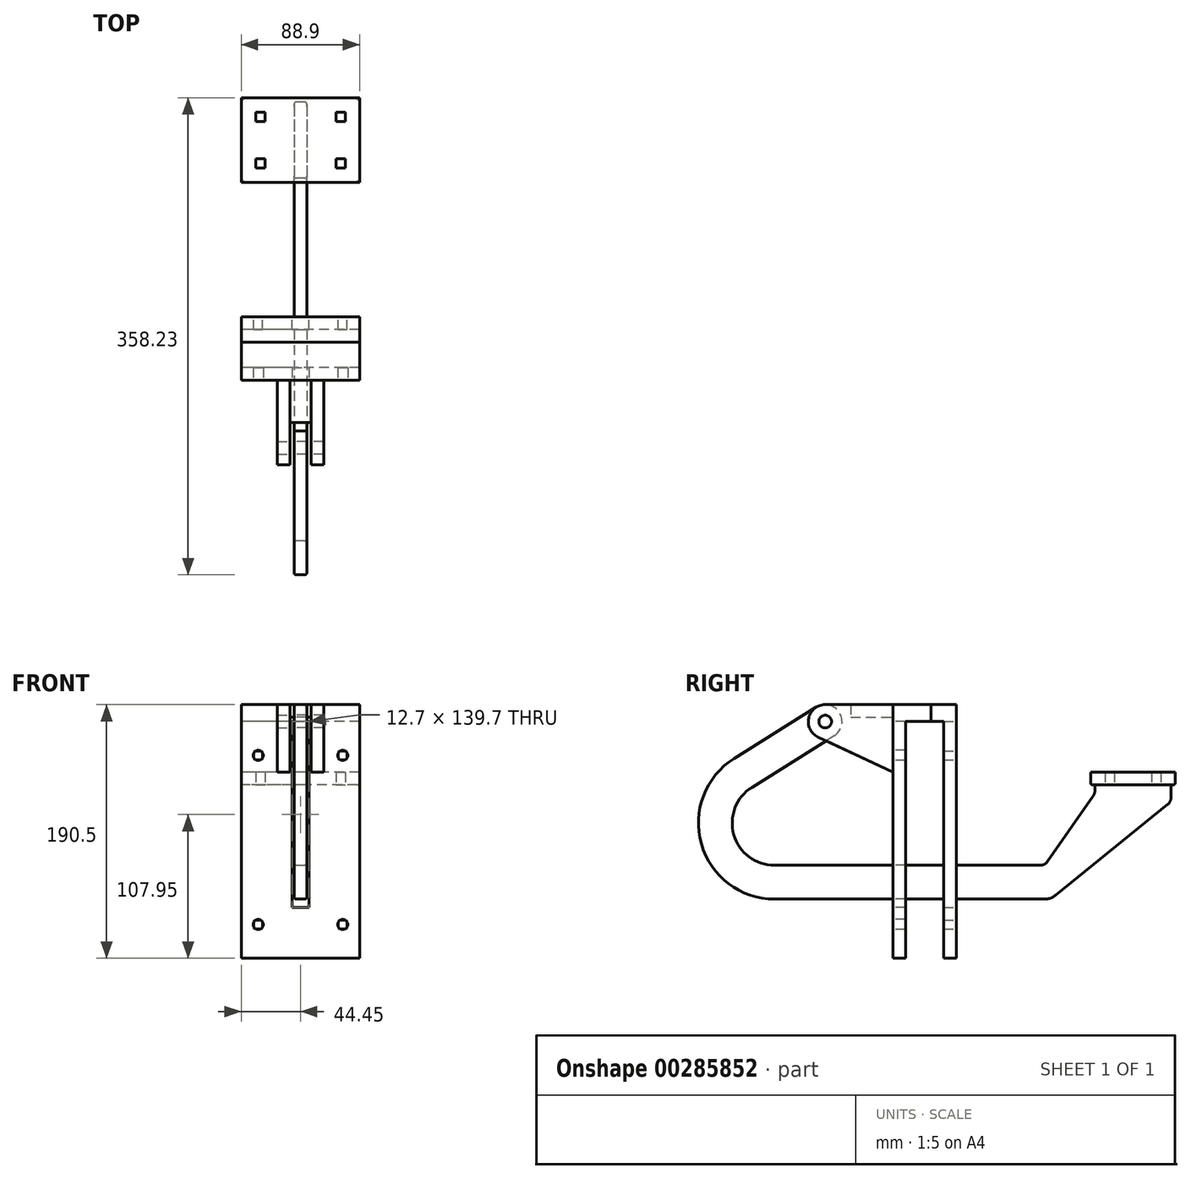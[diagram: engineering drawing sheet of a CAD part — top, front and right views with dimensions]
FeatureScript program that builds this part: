
annotation { "Feature Type Name" : "Feature", "Feature Type Description" : "" }
export const myFeature = defineFeature(function(context is Context, id is Id, definition is map)
    precondition{}
    {
        {
            var Q0;
            Q0=qCreatedBy(makeId("Right.planeOp"),FACE);
            var sketch = newSketch(context, id + "F0", { "sketchPlane" : qUnion([Q0])});
            skLineSegment(sketch, "E0.bottom", {"start": v(165.1, -133.35) * mm, "end": v(-38.1, -133.35) * mm});
            skLineSegment(sketch, "E0.top", {"start": v(161.65, -107.95) * mm, "end": v(-38.1, -107.95) * mm});
            skLineSegment(sketch, "E0.left", {"start": v(169.6, -133.35) * mm, "end": v(169.6, -132.53) * mm});
            skPoint(sketch, "E0.middle", {"position": v(0, 0) * mm});
            skLineSegment(sketch, "E1.bottom", {"start": v(262.98, -47.62) * mm, "end": v(199.48, -47.62) * mm});
            skLineSegment(sketch, "E1.top", {"start": v(262.98, -38.1) * mm, "end": v(199.48, -38.1) * mm});
            skLineSegment(sketch, "E1.left", {"start": v(262.98, -47.62) * mm, "end": v(262.98, -38.1) * mm});
            skLineSegment(sketch, "E1.right", {"start": v(199.48, -47.62) * mm, "end": v(199.48, -38.1) * mm});
            skPoint(sketch, "E1.middle", {"position": v(231.23, -42.86) * mm});
            skLineSegment(sketch, "E2.bottom", {"start": v(60.33, -177.8) * mm, "end": v(50.8, -177.8) * mm});
            skLineSegment(sketch, "E2.top", {"start": v(60.33, 12.7) * mm, "end": v(50.8, 12.7) * mm});
            skLineSegment(sketch, "E2.left", {"start": v(60.33, -177.8) * mm, "end": v(60.33, 12.7) * mm});
            skLineSegment(sketch, "E2.right", {"start": v(50.8, -177.8) * mm, "end": v(50.8, 12.7) * mm});
            skPoint(sketch, "E2.middle", {"position": v(55.56, -82.55) * mm});
            skArc(sketch, "E3", {"start": v(6.73, -10.77) * mm, "mid": v(-0.74, 12.68) * mm, "end": v(-5.43, -11.48) * mm});
            skLineSegment(sketch, "E4", {"start": v(0, 12.7) * mm, "end": v(50.8, 12.7) * mm});
            skLineSegment(sketch, "E5", {"start": v(50.8, -38.1) * mm, "end": v(-5.43, -11.48) * mm});
            skLineSegment(sketch, "E6.0", {"start": v(6.73, -10.77) * mm, "end": v(-54.92, -49.27) * mm});
            skLineSegment(sketch, "E7", {"start": v(257.45, -62.23) * mm, "end": v(173.1, -130.52) * mm});
            skPoint(sketch, "E8.visualSharp", {"position": v(169.6, -133.35) * mm});
            skArc(sketch, "E8.filletArc", {"start": v(165.1, -133.35) * mm, "mid": v(169.34, -132.62) * mm, "end": v(173.1, -130.52) * mm});
            skLineSegment(sketch, "E9", {"start": v(166.85, -105.24) * mm, "end": v(201.51, -55.61) * mm});
            skPoint(sketch, "E10.visualSharp", {"position": v(164.96, -107.95) * mm});
            skArc(sketch, "E10.filletArc", {"start": v(161.65, -107.95) * mm, "mid": v(164.58, -107.23) * mm, "end": v(166.85, -105.24) * mm});
            skLineSegment(sketch, "E11.bottom", {"start": v(50.8, 3.18) * mm, "end": v(19.05, 3.18) * mm});
            skLineSegment(sketch, "E11.top", {"start": v(50.8, 12.7) * mm, "end": v(19.05, 12.7) * mm});
            skLineSegment(sketch, "E11.left", {"start": v(50.8, 3.18) * mm, "end": v(50.8, 12.7) * mm});
            skLineSegment(sketch, "E11.right", {"start": v(19.05, 3.18) * mm, "end": v(19.05, 12.7) * mm});
            skPoint(sketch, "E11.middle", {"position": v(34.93, 7.94) * mm});
            skLineSegment(sketch, "E12", {"start": v(-6.73, 10.77) * mm, "end": v(-68.37, -27.73) * mm});
            skPoint(sketch, "E13.visualSharp", {"position": v(-148.88, -107.95) * mm});
            skArc(sketch, "E13.filletArc", {"start": v(-54.92, -49.27) * mm, "mid": v(-68.62, -84.95) * mm, "end": v(-38.1, -107.95) * mm});
            skPoint(sketch, "E14.visualSharp", {"position": v(-237.5, -133.35) * mm});
            skArc(sketch, "E14.filletArc", {"start": v(-68.37, -27.73) * mm, "mid": v(-93.04, -91.95) * mm, "end": v(-38.1, -133.35) * mm});
            skLineSegment(sketch, "E15", {"start": v(60.33, 0) * mm, "end": v(79.38, 0) * mm});
            skLineSegment(sketch, "E16", {"start": v(79.38, 0) * mm, "end": v(79.38, 12.7) * mm});
            skLineSegment(sketch, "E17", {"start": v(79.38, 12.7) * mm, "end": v(60.33, 12.7) * mm});
            skLineSegment(sketch, "E18", {"start": v(187.89, -47.62) * mm, "end": v(274.63, -47.62) * mm, "construction": true});
            skLineSegment(sketch, "E19", {"start": v(259.8, -57.3) * mm, "end": v(259.8, -47.62) * mm});
            skLineSegment(sketch, "E20", {"start": v(202.66, -51.98) * mm, "end": v(202.66, -47.62) * mm});
            skLineSegment(sketch, "E21", {"start": v(202.66, -47.62) * mm, "end": v(199.48, -47.62) * mm, "construction": true});
            skPoint(sketch, "E22.visualSharp", {"position": v(259.8, -60.32) * mm});
            skArc(sketch, "E22.filletArc", {"start": v(257.45, -62.23) * mm, "mid": v(259.19, -60.03) * mm, "end": v(259.8, -57.3) * mm});
            skPoint(sketch, "E23.visualSharp", {"position": v(202.66, -53.97) * mm});
            skArc(sketch, "E23.filletArc", {"start": v(201.51, -55.61) * mm, "mid": v(202.36, -53.88) * mm, "end": v(202.66, -51.98) * mm});
            skCircle(sketch, "E24", {"center": v(0, 0) * mm, "radius": 4.78 * mm});
            skSolve(sketch);
        }
        {
            var Q0;
            {var subQ12=sQuery(id+"F0.wireOp",EDGE,"ojWnpXek-w9QP-OmrP-CbvC-UmweZ5DEQAdM");Q0=makeQuery(id+"F0.imprint","IMPRINT",FACE,{"disambiguationData":[TD([[makeQuery(id+"F0.imprint","IMPRINT",EDGE,{"derivedFrom":subQ12}),1.0]])]});}
            var Q1;
            Q1=makeQuery(id+"F0.imprint","IMPRINT",FACE,{"disambiguationData":[TD([[makeQuery(id+"F0.imprint","IMPRINT",EDGE,{"derivedFrom":sQuery(id+"F0.wireOp",EDGE,"ZWXedtB1-B3w1-zQnL-7TSo-fpOSPy3oLPJk")}),-1.0]])]});
            var Q2;
            {var subQ5=sQuery(id+"F0.wireOp",EDGE,"zfqev4Cs-Zl6h-Keqt-t5Zp-NvnRYcSyTW9s");Q2=makeQuery(id+"F0.imprint","IMPRINT",FACE,{"disambiguationData":[TD([[makeQuery(id+"F0.imprint","IMPRINT",EDGE,{"derivedFrom":subQ5}),-1.0]])]});}
            var Q3;
            {var subQ0=sQuery(id+"F0.wireOp",EDGE,"E2.left");var subQ1=sQuery(id+"F0.wireOp",EDGE,"E0.bottom");var subQ2=makeQuery(id+"F0.imprint","INTERSECT",VERTEX,{"derivedFrom":[subQ1,subQ0]});Q3=makeQuery(id+"F0.imprint","IMPRINT",FACE,{"disambiguationData":[TD([[makeQuery(id+"F0.imprint","IMPRINT",EDGE,{"disambiguationData":[TD([[subQ2,-1.0]])],"derivedFrom":subQ1}),-1.0]])]});}
            var Q4;
            {var subQ7=sQuery(id+"F0.wireOp",EDGE,"E12");Q4=makeQuery(id+"F0.imprint","IMPRINT",FACE,{"disambiguationData":[TD([[makeQuery(id+"F0.imprint","IMPRINT",EDGE,{"derivedFrom":subQ7}),1.0]])]});}
            var Q5;
            {var subQ4=sQuery(id+"F0.wireOp",EDGE,"E7");Q5=makeQuery(id+"F0.imprint","IMPRINT",FACE,{"disambiguationData":[TD([[makeQuery(id+"F0.imprint","IMPRINT",EDGE,{"derivedFrom":subQ4}),-1.0]])]});}
            var Q6;
            Q6=makeQuery(id+"F0.imprint","IMPRINT",FACE,{"disambiguationData":[TD([[makeQuery(id+"F0.imprint","IMPRINT",EDGE,{"derivedFrom":sQuery(id+"F0.wireOp",EDGE,"E24")}),-1.0]])]});
            extrude(context, id + "F1", {"entities" : qUnion([Q0, Q1, Q2, Q3, Q4, Q5, Q6]), "endBound" : BoundingType.SYMMETRIC, "depth" : 9.52 * mm});
        }
        {
            var Q0;
            Q0=makeQuery(id+"F1.opExtrude","CAP_FACE",FACE,{"disambiguationData":[OSD([sQuery(id+"F0.wireOp",EDGE,"E0.bottom"),sQuery(id+"F0.wireOp",EDGE,"E0.top"),sQuery(id+"F0.wireOp",EDGE,"E1.bottom"),sQuery(id+"F0.wireOp",EDGE,"E3"),sQuery(id+"F0.wireOp",EDGE,"E6.0"),sQuery(id+"F0.wireOp",EDGE,"E7"),sQuery(id+"F0.wireOp",EDGE,"E8.filletArc"),sQuery(id+"F0.wireOp",EDGE,"E9"),sQuery(id+"F0.wireOp",EDGE,"E10.filletArc"),sQuery(id+"F0.wireOp",EDGE,"E12"),sQuery(id+"F0.wireOp",EDGE,"E13.filletArc"),sQuery(id+"F0.wireOp",EDGE,"E14.filletArc"),sQuery(id+"F0.wireOp",EDGE,"E19"),sQuery(id+"F0.wireOp",EDGE,"E20"),sQuery(id+"F0.wireOp",EDGE,"E22.filletArc"),sQuery(id+"F0.wireOp",EDGE,"E23.filletArc"),sQuery(id+"F0.wireOp",EDGE,"E24")])],"isStart":false});
            cPlane(context, id + "F2", {"entities" : qUnion([Q0]), "cplaneType" : CPlaneType.OFFSET, "offset" : 3.17 * mm, "width" : 152.4 * mm, "height" : 152.4 * mm});
        }
        {
            var Q0;
            Q0=makeQuery(id+"F1.opExtrude","CAP_FACE",FACE,{"disambiguationData":[OSD([sQuery(id+"F0.wireOp",EDGE,"E0.bottom"),sQuery(id+"F0.wireOp",EDGE,"E0.top"),sQuery(id+"F0.wireOp",EDGE,"E1.bottom"),sQuery(id+"F0.wireOp",EDGE,"E3"),sQuery(id+"F0.wireOp",EDGE,"E6.0"),sQuery(id+"F0.wireOp",EDGE,"E7"),sQuery(id+"F0.wireOp",EDGE,"E8.filletArc"),sQuery(id+"F0.wireOp",EDGE,"E9"),sQuery(id+"F0.wireOp",EDGE,"E10.filletArc"),sQuery(id+"F0.wireOp",EDGE,"E12"),sQuery(id+"F0.wireOp",EDGE,"E13.filletArc"),sQuery(id+"F0.wireOp",EDGE,"E14.filletArc"),sQuery(id+"F0.wireOp",EDGE,"E19"),sQuery(id+"F0.wireOp",EDGE,"E20"),sQuery(id+"F0.wireOp",EDGE,"E22.filletArc"),sQuery(id+"F0.wireOp",EDGE,"E23.filletArc"),sQuery(id+"F0.wireOp",EDGE,"E24")])],"isStart":true});
            cPlane(context, id + "F3", {"entities" : qUnion([Q0]), "cplaneType" : CPlaneType.OFFSET, "offset" : 3.17 * mm, "width" : 152.4 * mm, "height" : 152.4 * mm});
        }
        {
            var Q0;
            Q0=qCreatedBy(id+"F2.planeOp",FACE);
            var sketch = newSketch(context, id + "F4", { "sketchPlane" : qUnion([Q0])});
            skLineSegment(sketch, "E25.0", {"start": v(0, 12.7) * mm, "end": v(50.8, 12.7) * mm});
            skArc(sketch, "E25.1", {"start": v(0, 12.7) * mm, "mid": v(-12.4, 2.78) * mm, "end": v(-5.43, -11.48) * mm});
            skLineSegment(sketch, "E25.2", {"start": v(50.8, -38.1) * mm, "end": v(-5.43, -11.48) * mm});
            skLineSegment(sketch, "E25.3", {"start": v(50.8, -177.8) * mm, "end": v(50.8, 12.7) * mm});
            skCircle(sketch, "E26.0", {"center": v(0, 0) * mm, "radius": 4.78 * mm});
            skSolve(sketch);
        }
        {
            var Q0;
            {var subQ1=sQuery(id+"F4.wireOp",EDGE,"E25.0");Q0=makeQuery(id+"F4.imprint","IMPRINT",FACE,{"disambiguationData":[TD([[makeQuery(id+"F4.imprint","IMPRINT",EDGE,{"derivedFrom":subQ1}),-1.0]])]});}
            extrude(context, id + "F5", {"entities" : qUnion([Q0]), "depth" : 9.52 * mm});
        }
        {
            var Q0;
            Q0=makeQuery(id+"F5.opExtrude","SWEPT_BODY",BODY,{"disambiguationData":[OSD([sQuery(id+"F4.wireOp",EDGE,"E25.0"),sQuery(id+"F4.wireOp",EDGE,"E25.1"),sQuery(id+"F4.wireOp",EDGE,"E25.2"),sQuery(id+"F4.wireOp",EDGE,"E25.3"),sQuery(id+"F4.wireOp",EDGE,"E26.0")])]});
            var Q1;
            Q1=qCreatedBy(makeId("Right.planeOp"),FACE);
            mirror(context, id + "F6", {"entities" : qUnion([Q0]), "mirrorPlane" : qUnion([Q1])});
        }
        {
            var Q0;
            {var subQ1=sQuery(id+"F0.wireOp",EDGE,"E2.top");Q0=makeQuery(id+"F0.imprint","IMPRINT",FACE,{"disambiguationData":[TD([[makeQuery(id+"F0.imprint","IMPRINT",EDGE,{"derivedFrom":subQ1}),1.0]])]});}
            var Q1;
            Q1=makeQuery(id+"F0.imprint","IMPRINT",FACE,{"disambiguationData":[TD([[makeQuery(id+"F0.imprint","IMPRINT",EDGE,{"derivedFrom":sQuery(id+"F0.wireOp",EDGE,"E1.top")}),1.0]])]});
            var Q2;
            {var subQ5=sQuery(id+"F0.wireOp",EDGE,"E2.bottom");Q2=makeQuery(id+"F0.imprint","IMPRINT",FACE,{"disambiguationData":[TD([[makeQuery(id+"F0.imprint","IMPRINT",EDGE,{"derivedFrom":subQ5}),-1.0]])]});}
            var Q3;
            {var subQ0=sQuery(id+"F0.wireOp",EDGE,"E2.left");var subQ1=sQuery(id+"F0.wireOp",EDGE,"E0.bottom");var subQ2=makeQuery(id+"F0.imprint","INTERSECT",VERTEX,{"derivedFrom":[subQ1,subQ0]});Q3=makeQuery(id+"F0.imprint","IMPRINT",FACE,{"disambiguationData":[TD([[makeQuery(id+"F0.imprint","IMPRINT",EDGE,{"disambiguationData":[TD([[subQ2,-1.0]])],"derivedFrom":subQ1}),-1.0]])]});}
            var Q4;
            {var subQ2=sQuery(id+"F0.wireOp",EDGE,"E15");Q4=makeQuery(id+"F0.imprint","IMPRINT",FACE,{"disambiguationData":[TD([[makeQuery(id+"F0.imprint","IMPRINT",EDGE,{"derivedFrom":subQ2}),1.0]])]});}
            extrude(context, id + "F7", {"entities" : qUnion([Q0, Q1, Q2, Q3, Q4]), "endBound" : BoundingType.SYMMETRIC, "depth" : 88.9 * mm});
        }
        {
            var Q0;
            Q0=qCreatedBy(makeId("Top.planeOp"),FACE);
            var sketch = newSketch(context, id + "F8", { "sketchPlane" : qUnion([Q0])});
            skLineSegment(sketch, "E27.bottom", {"start": v(7.94, -50.8) * mm, "end": v(-7.94, -50.8) * mm});
            skLineSegment(sketch, "E27.top", {"start": v(7.94, 50.8) * mm, "end": v(-7.94, 50.8) * mm});
            skLineSegment(sketch, "E27.left", {"start": v(7.94, -50.8) * mm, "end": v(7.94, 50.8) * mm});
            skLineSegment(sketch, "E27.right", {"start": v(-7.94, -50.8) * mm, "end": v(-7.94, 50.8) * mm});
            skPoint(sketch, "E27.middle", {"position": v(0, 0) * mm});
            skSolve(sketch);
        }
        {
            var Q0;
            Q0=qCreatedBy(makeId("Front.planeOp"),FACE);
            var sketch = newSketch(context, id + "F9", { "sketchPlane" : qUnion([Q0])});
            skLineSegment(sketch, "E28.bottom", {"start": v(-6.35, 0) * mm, "end": v(6.35, 0) * mm});
            skLineSegment(sketch, "E28.top", {"start": v(-6.35, -139.7) * mm, "end": v(6.35, -139.7) * mm});
            skLineSegment(sketch, "E28.left", {"start": v(-6.35, 0) * mm, "end": v(-6.35, -139.7) * mm});
            skLineSegment(sketch, "E28.right", {"start": v(6.35, 0) * mm, "end": v(6.35, -139.7) * mm});
            skPoint(sketch, "E28.middle", {"position": v(0, -69.85) * mm});
            skSolve(sketch);
        }
        {
            var Q0;
            Q0=qSketchRegion(id+"F9",true);
            extrude(context, id + "F10", {"entities" : qUnion([Q0]), "oppositeDirection" : true, "depth" : 76.2 * mm});
        }
        {
            var Q0;
            Q0=makeQuery(id+"F10.opExtrude","SWEPT_BODY",BODY,{"disambiguationData":[OSD([sQuery(id+"F9.wireOp",EDGE,"E28.bottom"),sQuery(id+"F9.wireOp",EDGE,"E28.top"),sQuery(id+"F9.wireOp",EDGE,"E28.left"),sQuery(id+"F9.wireOp",EDGE,"E28.right")])]});
            var Q1;
            Q1=makeQuery(id+"F5.opExtrude","SWEPT_BODY",BODY,{"disambiguationData":[OSD([sQuery(id+"F0.wireOp",EDGE,"E2.right"),sQuery(id+"F0.wireOp",EDGE,"E3"),sQuery(id+"F0.wireOp",EDGE,"E4"),sQuery(id+"F0.wireOp",EDGE,"E5"),sQuery(id+"F0.wireOp",EDGE,"ZWXedtB1-B3w1-zQnL-7TSo-fpOSPy3oLPJk")])]});
            var Q2;
            Q2=makeQuery(id+"F7.opExtrude","SWEPT_BODY",BODY,{"disambiguationData":[OSD([sQuery(id+"F0.wireOp",EDGE,"E2.bottom"),sQuery(id+"F0.wireOp",EDGE,"E2.top"),sQuery(id+"F0.wireOp",EDGE,"E2.left"),sQuery(id+"F0.wireOp",EDGE,"E2.right"),sQuery(id+"F0.wireOp",EDGE,"E11.left"),sQuery(id+"F0.wireOp",EDGE,"E15"),sQuery(id+"F0.wireOp",EDGE,"E16"),sQuery(id+"F0.wireOp",EDGE,"E17")])]});
            booleanBodies(context, id + "F11", {"operationType" : BooleanOperationType.SUBTRACTION, "tools" : qUnion([Q0]), "targets" : qUnion([Q1, Q2])});
        }
        {
            var Q0;
            Q0=makeQuery(id+"F0.imprint","IMPRINT",FACE,{"disambiguationData":[TD([[makeQuery(id+"F0.imprint","IMPRINT",EDGE,{"derivedFrom":sQuery(id+"F0.wireOp",EDGE,"E11.bottom")}),-1.0]])]});
            var Q1;
            Q1=makeQuery(id+"F5.opExtrude","CAP_FACE",FACE,{"disambiguationData":[OSD([sQuery(id+"F4.wireOp",EDGE,"E25.0"),sQuery(id+"F4.wireOp",EDGE,"E25.1"),sQuery(id+"F4.wireOp",EDGE,"E25.2"),sQuery(id+"F4.wireOp",EDGE,"E25.3"),sQuery(id+"F4.wireOp",EDGE,"E26.0")])],"isStart":true});
            var Q2;
            Q2=makeQuery(id+"F6.opPattern","COPY",FACE,{"derivedFrom":makeQuery(id+"F5.opExtrude","CAP_FACE",FACE,{"disambiguationData":[OSD([sQuery(id+"F4.wireOp",EDGE,"E25.0"),sQuery(id+"F4.wireOp",EDGE,"E25.1"),sQuery(id+"F4.wireOp",EDGE,"E25.2"),sQuery(id+"F4.wireOp",EDGE,"E25.3"),sQuery(id+"F4.wireOp",EDGE,"E26.0")])],"isStart":true}),"instanceName":"1"});
            extrude(context, id + "F12", {"entities" : qUnion([Q0]), "endBound" : BoundingType.UP_TO_SURFACE, "endBoundEntityFace" : qUnion([Q1]), "depth" : 12.7 * mm, "hasSecondDirection" : true, "secondDirectionBound" : SecondDirectionBoundingType.UP_TO_SURFACE, "secondDirectionOppositeDirection" : true, "secondDirectionBoundEntityFace" : qUnion([Q2]), "secondDirectionDepth" : 25.4 * mm});
        }
        {
            var Q0;
            Q0=makeQuery(id+"F1.opExtrude","CAP_EDGE",EDGE,{"disambiguationData":[OSD([sQuery(id+"F0.wireOp",EDGE,"E10.filletArc")])],"isStart":false});
            var Q1;
            Q1=makeQuery(id+"F1.opExtrude","CAP_EDGE",EDGE,{"disambiguationData":[OSD([sQuery(id+"F0.wireOp",EDGE,"E0.top")])],"isStart":false});
            var Q2;
            Q2=makeQuery(id+"F1.opExtrude","CAP_EDGE",EDGE,{"disambiguationData":[OSD([sQuery(id+"F0.wireOp",EDGE,"E13.filletArc")])],"isStart":false});
            var Q3;
            Q3=makeQuery(id+"F1.opExtrude","CAP_EDGE",EDGE,{"disambiguationData":[OSD([sQuery(id+"F0.wireOp",EDGE,"E6.0")])],"isStart":false});
            var Q4;
            Q4=makeQuery(id+"F1.opExtrude","CAP_EDGE",EDGE,{"disambiguationData":[OSD([sQuery(id+"F0.wireOp",EDGE,"E12")])],"isStart":false});
            var Q5;
            Q5=makeQuery(id+"F1.opExtrude","CAP_EDGE",EDGE,{"disambiguationData":[OSD([sQuery(id+"F0.wireOp",EDGE,"E14.filletArc")])],"isStart":false});
            var Q6;
            Q6=makeQuery(id+"F1.opExtrude","CAP_EDGE",EDGE,{"disambiguationData":[OSD([sQuery(id+"F0.wireOp",EDGE,"E0.bottom")])],"isStart":false});
            var Q7;
            Q7=makeQuery(id+"F1.opExtrude","CAP_EDGE",EDGE,{"disambiguationData":[OSD([sQuery(id+"F0.wireOp",EDGE,"E8.filletArc")])],"isStart":false});
            var Q8;
            Q8=makeQuery(id+"F1.opExtrude","CAP_EDGE",EDGE,{"disambiguationData":[OSD([sQuery(id+"F0.wireOp",EDGE,"E7")])],"isStart":false});
            var Q9;
            Q9=makeQuery(id+"F1.opExtrude","CAP_EDGE",EDGE,{"disambiguationData":[OSD([sQuery(id+"F0.wireOp",EDGE,"E3")])],"isStart":false});
            var Q10;
            Q10=makeQuery(id+"F1.opExtrude","CAP_EDGE",EDGE,{"disambiguationData":[OSD([sQuery(id+"F0.wireOp",EDGE,"nBXHWYCG-ocgf-b43t-3LkW-cHly0ma2DKAZ")])],"isStart":false});
            var Q11;
            Q11=makeQuery(id+"F1.opExtrude","CAP_EDGE",EDGE,{"disambiguationData":[OSD([sQuery(id+"F0.wireOp",EDGE,"E12")])],"isStart":true});
            var Q12;
            Q12=makeQuery(id+"F1.opExtrude","CAP_EDGE",EDGE,{"disambiguationData":[OSD([sQuery(id+"F0.wireOp",EDGE,"E14.filletArc")])],"isStart":true});
            var Q13;
            Q13=makeQuery(id+"F1.opExtrude","CAP_EDGE",EDGE,{"disambiguationData":[OSD([sQuery(id+"F0.wireOp",EDGE,"E3")])],"isStart":true});
            var Q14;
            Q14=makeQuery(id+"F1.opExtrude","CAP_EDGE",EDGE,{"disambiguationData":[OSD([sQuery(id+"F0.wireOp",EDGE,"E6.0")])],"isStart":true});
            var Q15;
            Q15=makeQuery(id+"F1.opExtrude","CAP_EDGE",EDGE,{"disambiguationData":[OSD([sQuery(id+"F0.wireOp",EDGE,"E13.filletArc")])],"isStart":true});
            var Q16;
            Q16=makeQuery(id+"F1.opExtrude","CAP_EDGE",EDGE,{"disambiguationData":[OSD([sQuery(id+"F0.wireOp",EDGE,"E0.top")])],"isStart":true});
            var Q17;
            Q17=makeQuery(id+"F1.opExtrude","CAP_EDGE",EDGE,{"disambiguationData":[OSD([sQuery(id+"F0.wireOp",EDGE,"E10.filletArc")])],"isStart":true});
            var Q18;
            Q18=makeQuery(id+"F1.opExtrude","CAP_EDGE",EDGE,{"disambiguationData":[OSD([sQuery(id+"F0.wireOp",EDGE,"E9")])],"isStart":true});
            var Q19;
            Q19=makeQuery(id+"F1.opExtrude","CAP_EDGE",EDGE,{"disambiguationData":[OSD([sQuery(id+"F0.wireOp",EDGE,"nBXHWYCG-ocgf-b43t-3LkW-cHly0ma2DKAZ")])],"isStart":true});
            fillet(context, id + "F13", {"entities" : qUnion([Q0, Q1, Q2, Q3, Q4, Q5, Q6, Q7, Q8, Q9, Q10, Q11, Q12, Q13, Q14, Q15, Q16, Q17, Q18, Q19]), "radius" : 1.59 * mm, "tangentPropagation" : true, "allowEdgeOverflow" : false});
        }
        {
            var Q0;
            Q0=makeQuery(id+"F7.opExtrude","CAP_EDGE",EDGE,{"disambiguationData":[OSD([sQuery(id+"F0.wireOp",EDGE,"E1.bottom")])],"isStart":true});
            var Q1;
            Q1=makeQuery(id+"F7.opExtrude","SWEPT_EDGE",EDGE,{"disambiguationData":[OSD([sQuery(id+"F0.wireOp",EDGE,"E1.bottom"),sQuery(id+"F0.wireOp",EDGE,"E1.right")])]});
            var Q2;
            Q2=makeQuery(id+"F7.opExtrude","CAP_EDGE",EDGE,{"disambiguationData":[OSD([sQuery(id+"F0.wireOp",EDGE,"E1.bottom")])],"isStart":false});
            var Q3;
            Q3=makeQuery(id+"F7.opExtrude","SWEPT_EDGE",EDGE,{"disambiguationData":[OSD([sQuery(id+"F0.wireOp",EDGE,"E1.bottom"),sQuery(id+"F0.wireOp",EDGE,"E1.left")])]});
            fillet(context, id + "F14", {"entities" : qUnion([Q0, Q1, Q2, Q3]), "radius" : 1.59 * mm, "tangentPropagation" : true, "allowEdgeOverflow" : false});
        }
        {
            var Q0;
            Q0=makeQuery(id+"F7.opExtrude","SWEPT_FACE",FACE,{"disambiguationData":[OSD([sQuery(id+"F0.wireOp",EDGE,"E1.bottom")])]});
            var sketch = newSketch(context, id + "F15", { "sketchPlane" : qUnion([Q0])});
            skLineSegment(sketch, "E29.bottom", {"start": v(42.86, -261.4) * mm, "end": v(-42.86, -261.4) * mm, "construction": true});
            skLineSegment(sketch, "E29.top", {"start": v(42.86, -201.07) * mm, "end": v(-42.86, -201.07) * mm, "construction": true});
            skLineSegment(sketch, "E29.left", {"start": v(42.86, -261.4) * mm, "end": v(42.86, -201.07) * mm, "construction": true});
            skLineSegment(sketch, "E29.right", {"start": v(-42.86, -261.4) * mm, "end": v(-42.86, -201.07) * mm, "construction": true});
            skPoint(sketch, "E29.middle", {"position": v(0, -231.23) * mm});
            skLineSegment(sketch, "E30.0", {"start": v(36.51, -213.77) * mm, "end": v(-36.51, -213.77) * mm, "construction": true});
            skLineSegment(sketch, "E31.0", {"start": v(30.16, -264.57) * mm, "end": v(30.16, -204.24) * mm, "construction": true});
            skLineSegment(sketch, "E32.0", {"start": v(36.51, -248.7) * mm, "end": v(-36.51, -248.7) * mm, "construction": true});
            skLineSegment(sketch, "E33.0", {"start": v(-30.16, -264.57) * mm, "end": v(-30.16, -204.24) * mm, "construction": true});
            skLineSegment(sketch, "E34.bottom", {"start": v(33.6, -252.12) * mm, "end": v(-33.6, -252.12) * mm, "construction": true});
            skLineSegment(sketch, "E34.top", {"start": v(33.6, -210.34) * mm, "end": v(-33.6, -210.34) * mm, "construction": true});
            skLineSegment(sketch, "E34.left", {"start": v(33.6, -252.12) * mm, "end": v(33.6, -210.34) * mm, "construction": true});
            skLineSegment(sketch, "E34.right", {"start": v(-33.6, -252.12) * mm, "end": v(-33.6, -210.34) * mm, "construction": true});
            skLineSegment(sketch, "E35.bottom", {"start": v(26.73, -245.26) * mm, "end": v(-26.73, -245.26) * mm, "construction": true});
            skLineSegment(sketch, "E35.top", {"start": v(26.73, -217.2) * mm, "end": v(-26.73, -217.2) * mm, "construction": true});
            skLineSegment(sketch, "E35.left", {"start": v(26.73, -245.26) * mm, "end": v(26.73, -217.2) * mm, "construction": true});
            skLineSegment(sketch, "E35.right", {"start": v(-26.73, -245.26) * mm, "end": v(-26.73, -217.2) * mm, "construction": true});
            skLineSegment(sketch, "E36.bottom", {"start": v(-33.6, -210.34) * mm, "end": v(-26.73, -210.34) * mm});
            skLineSegment(sketch, "E36.top", {"start": v(-33.6, -217.2) * mm, "end": v(-26.73, -217.2) * mm});
            skLineSegment(sketch, "E36.left", {"start": v(-33.6, -210.34) * mm, "end": v(-33.6, -217.2) * mm});
            skLineSegment(sketch, "E36.right", {"start": v(-26.73, -210.34) * mm, "end": v(-26.73, -217.2) * mm});
            skLineSegment(sketch, "E37.bottom", {"start": v(33.6, -210.34) * mm, "end": v(26.73, -210.34) * mm});
            skLineSegment(sketch, "E37.top", {"start": v(33.6, -217.2) * mm, "end": v(26.73, -217.2) * mm});
            skLineSegment(sketch, "E37.left", {"start": v(33.6, -210.34) * mm, "end": v(33.6, -217.2) * mm});
            skLineSegment(sketch, "E37.right", {"start": v(26.73, -210.34) * mm, "end": v(26.73, -217.2) * mm});
            skLineSegment(sketch, "E38.bottom", {"start": v(26.73, -245.26) * mm, "end": v(33.6, -245.26) * mm});
            skLineSegment(sketch, "E38.top", {"start": v(26.73, -252.12) * mm, "end": v(33.6, -252.12) * mm});
            skLineSegment(sketch, "E38.left", {"start": v(26.73, -245.26) * mm, "end": v(26.73, -252.12) * mm});
            skLineSegment(sketch, "E38.right", {"start": v(33.6, -245.26) * mm, "end": v(33.6, -252.12) * mm});
            skLineSegment(sketch, "E39.bottom", {"start": v(-26.73, -245.26) * mm, "end": v(-33.6, -245.26) * mm});
            skLineSegment(sketch, "E39.top", {"start": v(-26.73, -252.12) * mm, "end": v(-33.6, -252.12) * mm});
            skLineSegment(sketch, "E39.left", {"start": v(-26.73, -245.26) * mm, "end": v(-26.73, -252.12) * mm});
            skLineSegment(sketch, "E39.right", {"start": v(-33.6, -245.26) * mm, "end": v(-33.6, -252.12) * mm});
            skSolve(sketch);
        }
        {
            var Q0;
            Q0=makeQuery(id+"F15.imprint","IMPRINT",FACE,{"disambiguationData":[TD([[makeQuery(id+"F15.imprint","IMPRINT",EDGE,{"derivedFrom":sQuery(id+"F15.wireOp",EDGE,"E36.bottom")}),-1.0]])]});
            var Q1;
            Q1=makeQuery(id+"F15.imprint","IMPRINT",FACE,{"disambiguationData":[TD([[makeQuery(id+"F15.imprint","IMPRINT",EDGE,{"derivedFrom":sQuery(id+"F15.wireOp",EDGE,"E37.bottom")}),1.0]])]});
            var Q2;
            Q2=makeQuery(id+"F15.imprint","IMPRINT",FACE,{"disambiguationData":[TD([[makeQuery(id+"F15.imprint","IMPRINT",EDGE,{"derivedFrom":sQuery(id+"F15.wireOp",EDGE,"E39.bottom")}),1.0]])]});
            var Q3;
            Q3=makeQuery(id+"F15.imprint","IMPRINT",FACE,{"disambiguationData":[TD([[makeQuery(id+"F15.imprint","IMPRINT",EDGE,{"derivedFrom":sQuery(id+"F15.wireOp",EDGE,"E38.bottom")}),-1.0]])]});
            extrude(context, id + "F16", {"entities" : qUnion([Q0, Q1, Q2, Q3]), "operationType" : NewBodyOperationType.REMOVE, "oppositeDirection" : true, "depth" : 9.52 * mm});
        }
        {
            var Q0;
            {var subQ5=sQuery(id+"F0.wireOp",EDGE,"E4");var subQ7=sQuery(id+"F0.wireOp",EDGE,"E2.right");var subQ8=sQuery(id+"F0.wireOp",EDGE,"E11.left");Q0=makeQuery(id+"F12.boolean.opBoolean","SPLIT",FACE,{"disambiguationData":[TD([makeQuery(id+"F5.opExtrude","SWEPT_FACE",FACE,{"disambiguationData":[OSD([subQ5])]})])],"derivedFrom":makeQuery(id+"F9vXf4BlpSkugzr_3.opBoolean","MERGE",FACE,{"derivedFrom":[makeQuery(id+"F7.opExtrude","SWEPT_FACE",FACE,{"disambiguationData":[OSD([subQ7,subQ8])]}),makeQuery(id+"FLQFy2sVfI9G7pO_2.opExtrude","SWEPT_FACE",FACE,{"disambiguationData":[OSD([sQuery(id+"F8.wireOp",EDGE,"E27.top")])]})]})});}
            var sketch = newSketch(context, id + "F17", { "sketchPlane" : qUnion([Q0])});
            skLineSegment(sketch, "E40.bottom", {"start": v(31.75, -152.4) * mm, "end": v(-31.75, -152.4) * mm});
            skLineSegment(sketch, "E40.top", {"start": v(31.75, -25.4) * mm, "end": v(-31.75, -25.4) * mm});
            skLineSegment(sketch, "E40.left", {"start": v(31.75, -152.4) * mm, "end": v(31.75, -25.4) * mm});
            skLineSegment(sketch, "E40.right", {"start": v(-31.75, -152.4) * mm, "end": v(-31.75, -25.4) * mm});
            skPoint(sketch, "E40.middle", {"position": v(0, -88.9) * mm});
            skSolve(sketch);
        }
        {
            var Q0;
            Q0=sQuery(id+"F17.wireOp",VERTEX,"E40.left.start");
            var Q1;
            Q1=sQuery(id+"F17.wireOp",VERTEX,"E40.right.start");
            var Q2;
            Q2=sQuery(id+"F17.wireOp",VERTEX,"E40.left.end");
            var Q3;
            Q3=sQuery(id+"F17.wireOp",VERTEX,"E40.right.end");
            var Q4;
            Q4=makeQuery(id+"F5.opExtrude","SWEPT_BODY",BODY,{"disambiguationData":[OSD([sQuery(id+"F0.wireOp",EDGE,"E2.right"),sQuery(id+"F0.wireOp",EDGE,"E3"),sQuery(id+"F0.wireOp",EDGE,"E4"),sQuery(id+"F0.wireOp",EDGE,"E5"),sQuery(id+"F0.wireOp",EDGE,"ZWXedtB1-B3w1-zQnL-7TSo-fpOSPy3oLPJk"),sQuery(id+"F0.wireOp",EDGE,"E11.bottom"),sQuery(id+"F0.wireOp",EDGE,"E11.right")])]});
            var Q5;
            Q5=makeQuery(id+"F7.opExtrude","SWEPT_BODY",BODY,{"disambiguationData":[OSD([sQuery(id+"F0.wireOp",EDGE,"E2.bottom"),sQuery(id+"F0.wireOp",EDGE,"E2.top"),sQuery(id+"F0.wireOp",EDGE,"E2.left"),sQuery(id+"F0.wireOp",EDGE,"E2.right"),sQuery(id+"F0.wireOp",EDGE,"E11.left"),sQuery(id+"F0.wireOp",EDGE,"E15"),sQuery(id+"F0.wireOp",EDGE,"E16"),sQuery(id+"F0.wireOp",EDGE,"E17")])]});
            hole(context, id + "F18", {"style" : HoleStyle.SIMPLE, "endStyle" : HoleEndStyle.THROUGH, "holeDiameter" : 7.62 * mm, "tappedDepth" : 12.7 * mm, "tapClearance" : 3, "locations" : qUnion([Q0, Q1, Q2, Q3]), "scope" : qUnion([Q4, Q5])});
        }
        {
            var Q0;
            {var subQ2=sQuery(id+"F0.wireOp",EDGE,"E15");Q0=makeQuery(id+"F0.imprint","IMPRINT",FACE,{"disambiguationData":[TD([[makeQuery(id+"F0.imprint","IMPRINT",EDGE,{"derivedFrom":subQ2}),1.0]])]});}
            extrude(context, id + "F19", {"entities" : qUnion([Q0]), "operationType" : NewBodyOperationType.ADD, "endBound" : BoundingType.SYMMETRIC, "depth" : 88.9 * mm});
        }
        {
            var Q0;
            Q0=qCreatedBy(makeId("Right.planeOp"),FACE);
            var sketch = newSketch(context, id + "F20", { "sketchPlane" : qUnion([Q0])});
            skLineSegment(sketch, "E41", {"start": v(88.9, 0) * mm, "end": v(88.9, -177.8) * mm});
            skLineSegment(sketch, "E42", {"start": v(88.9, -177.8) * mm, "end": v(98.43, -177.8) * mm});
            skLineSegment(sketch, "E43", {"start": v(98.43, -177.8) * mm, "end": v(98.43, 12.7) * mm});
            skLineSegment(sketch, "E44", {"start": v(79.38, 12.7) * mm, "end": v(98.43, 12.7) * mm});
            skLineSegment(sketch, "E45", {"start": v(60.33, -177.8) * mm, "end": v(135.86, -177.8) * mm, "construction": true});
            skLineSegment(sketch, "E46", {"start": v(79.38, 0) * mm, "end": v(88.9, 0) * mm});
            skLineSegment(sketch, "E47", {"start": v(79.38, 12.7) * mm, "end": v(79.38, 0) * mm});
            skSolve(sketch);
        }
        {
            var Q0;
            Q0 = qSketchRegion(id + "F20", true);
            var Q1;
            {var subQ0=sQuery(id+"F0.wireOp",EDGE,"E2.left");Q1=makeQuery(id+"F19.boolean.opBoolean","MERGE",FACE,{"derivedFrom":[makeQuery(id+"F7.opExtrude","CAP_FACE",FACE,{"disambiguationData":[OSD([sQuery(id+"F0.wireOp",EDGE,"E2.bottom"),sQuery(id+"F0.wireOp",EDGE,"E2.top"),subQ0,sQuery(id+"F0.wireOp",EDGE,"E2.right"),sQuery(id+"F0.wireOp",EDGE,"E11.left")])],"isStart":false}),makeQuery(id+"F19.opExtrude","CAP_FACE",FACE,{"disambiguationData":[OSD([subQ0,sQuery(id+"F0.wireOp",EDGE,"E15"),sQuery(id+"F0.wireOp",EDGE,"E16"),sQuery(id+"F0.wireOp",EDGE,"E17")])],"isStart":false})]});}
            var Q2;
            {var subQ0=sQuery(id+"F0.wireOp",EDGE,"E2.left");Q2=makeQuery(id+"F19.boolean.opBoolean","MERGE",FACE,{"derivedFrom":[makeQuery(id+"F7.opExtrude","CAP_FACE",FACE,{"disambiguationData":[OSD([sQuery(id+"F0.wireOp",EDGE,"E2.bottom"),sQuery(id+"F0.wireOp",EDGE,"E2.top"),subQ0,sQuery(id+"F0.wireOp",EDGE,"E2.right"),sQuery(id+"F0.wireOp",EDGE,"E11.left")])],"isStart":true}),makeQuery(id+"F19.opExtrude","CAP_FACE",FACE,{"disambiguationData":[OSD([subQ0,sQuery(id+"F0.wireOp",EDGE,"E15"),sQuery(id+"F0.wireOp",EDGE,"E16"),sQuery(id+"F0.wireOp",EDGE,"E17")])],"isStart":true})]});}
            extrude(context, id + "F21", {"entities" : qUnion([Q0]), "endBound" : BoundingType.UP_TO_SURFACE, "endBoundEntityFace" : qUnion([Q1]), "depth" : 25.4 * mm, "hasSecondDirection" : true, "secondDirectionBound" : SecondDirectionBoundingType.UP_TO_SURFACE, "secondDirectionOppositeDirection" : true, "secondDirectionBoundEntityFace" : qUnion([Q2]), "secondDirectionDepth" : 25.4 * mm});
        }
        {
            var Q0;
            Q0=makeQuery(id+"F21.opExtrude","SWEPT_FACE",FACE,{"disambiguationData":[OSD([sQuery(id+"F20.wireOp",EDGE,"E43")])]});
            var sketch = newSketch(context, id + "F22", { "sketchPlane" : qUnion([Q0])});
            skLineSegment(sketch, "E48.0", {"start": v(-6.35, 0) * mm, "end": v(-6.35, -139.7) * mm});
            skLineSegment(sketch, "E48.1", {"start": v(6.35, 0) * mm, "end": v(6.35, -139.7) * mm});
            skCircle(sketch, "E48.2", {"center": v(-31.75, -152.4) * mm, "radius": 3.81 * mm, "construction": true});
            skCircle(sketch, "E48.3", {"center": v(31.75, -25.4) * mm, "radius": 3.81 * mm, "construction": true});
            skCircle(sketch, "E48.4", {"center": v(-31.75, -25.4) * mm, "radius": 3.81 * mm, "construction": true});
            skLineSegment(sketch, "E48.5", {"start": v(6.35, -139.7) * mm, "end": v(-6.35, -139.7) * mm});
            skCircle(sketch, "E48.6", {"center": v(31.75, -152.4) * mm, "radius": 3.81 * mm, "construction": true});
            skLineSegment(sketch, "E49", {"start": v(-6.35, 0) * mm, "end": v(6.35, 0) * mm});
            skLineSegment(sketch, "E50", {"start": v(-31.75, -152.4) * mm, "end": v(31.75, -152.4) * mm, "construction": true});
            skLineSegment(sketch, "E51", {"start": v(-31.75, -25.4) * mm, "end": v(31.75, -25.4) * mm, "construction": true});
            skLineSegment(sketch, "E52.0", {"start": v(-37.2, -155.77) * mm, "end": v(37.2, -155.77) * mm, "construction": true});
            skLineSegment(sketch, "E52.2", {"start": v(-26.3, -28.77) * mm, "end": v(26.3, -28.77) * mm, "construction": true});
            skLineSegment(sketch, "E53.0", {"start": v(38.1, 6.35) * mm, "end": v(-38.1, 6.35) * mm, "construction": true});
            skLineSegment(sketch, "E53.1", {"start": v(38.1, -171.45) * mm, "end": v(38.1, 6.35) * mm, "construction": true});
            skLineSegment(sketch, "E53.2", {"start": v(-38.1, -171.45) * mm, "end": v(38.1, -171.45) * mm, "construction": true});
            skLineSegment(sketch, "E53.3", {"start": v(-38.1, 6.35) * mm, "end": v(-38.1, -171.45) * mm, "construction": true});
            skLineSegment(sketch, "E54.1", {"start": v(-35.13, -21.97) * mm, "end": v(35.13, -21.97) * mm, "construction": true});
            skLineSegment(sketch, "E54.3", {"start": v(-28.37, -148.97) * mm, "end": v(28.37, -148.97) * mm, "construction": true});
            skLineSegment(sketch, "E55.bottom", {"start": v(-35.13, -21.97) * mm, "end": v(-28.37, -21.97) * mm});
            skLineSegment(sketch, "E55.top", {"start": v(-35.13, -28.83) * mm, "end": v(-28.37, -28.83) * mm});
            skLineSegment(sketch, "E55.left", {"start": v(-35.13, -28.83) * mm, "end": v(-35.13, -21.97) * mm});
            skLineSegment(sketch, "E55.right", {"start": v(-28.37, -28.83) * mm, "end": v(-28.37, -21.97) * mm});
            skLineSegment(sketch, "E56.bottom", {"start": v(35.13, -148.97) * mm, "end": v(28.37, -148.97) * mm});
            skLineSegment(sketch, "E56.top", {"start": v(35.13, -155.83) * mm, "end": v(28.37, -155.83) * mm});
            skLineSegment(sketch, "E56.left", {"start": v(28.37, -155.83) * mm, "end": v(28.37, -148.97) * mm});
            skLineSegment(sketch, "E56.right", {"start": v(35.13, -155.83) * mm, "end": v(35.13, -148.97) * mm});
            skLineSegment(sketch, "E57.bottom", {"start": v(-28.37, -148.97) * mm, "end": v(-35.13, -148.97) * mm});
            skLineSegment(sketch, "E57.top", {"start": v(-28.37, -155.83) * mm, "end": v(-35.13, -155.83) * mm});
            skLineSegment(sketch, "E57.left", {"start": v(-28.37, -148.97) * mm, "end": v(-28.37, -155.83) * mm});
            skLineSegment(sketch, "E57.right", {"start": v(-35.13, -148.97) * mm, "end": v(-35.13, -155.83) * mm});
            skLineSegment(sketch, "E58.bottom", {"start": v(28.37, -21.97) * mm, "end": v(35.13, -21.97) * mm});
            skLineSegment(sketch, "E58.top", {"start": v(28.37, -28.83) * mm, "end": v(35.13, -28.83) * mm});
            skLineSegment(sketch, "E58.left", {"start": v(35.13, -21.97) * mm, "end": v(35.13, -28.83) * mm});
            skLineSegment(sketch, "E58.right", {"start": v(28.37, -21.97) * mm, "end": v(28.37, -28.83) * mm});
            skSolve(sketch);
        }
        {
            var Q0;
            Q0 = qSketchRegion(id + "F22", true);
            extrude(context, id + "F23", {"entities" : qUnion([Q0]), "operationType" : NewBodyOperationType.REMOVE, "oppositeDirection" : true, "depth" : 9.52 * mm});
        }
    });
